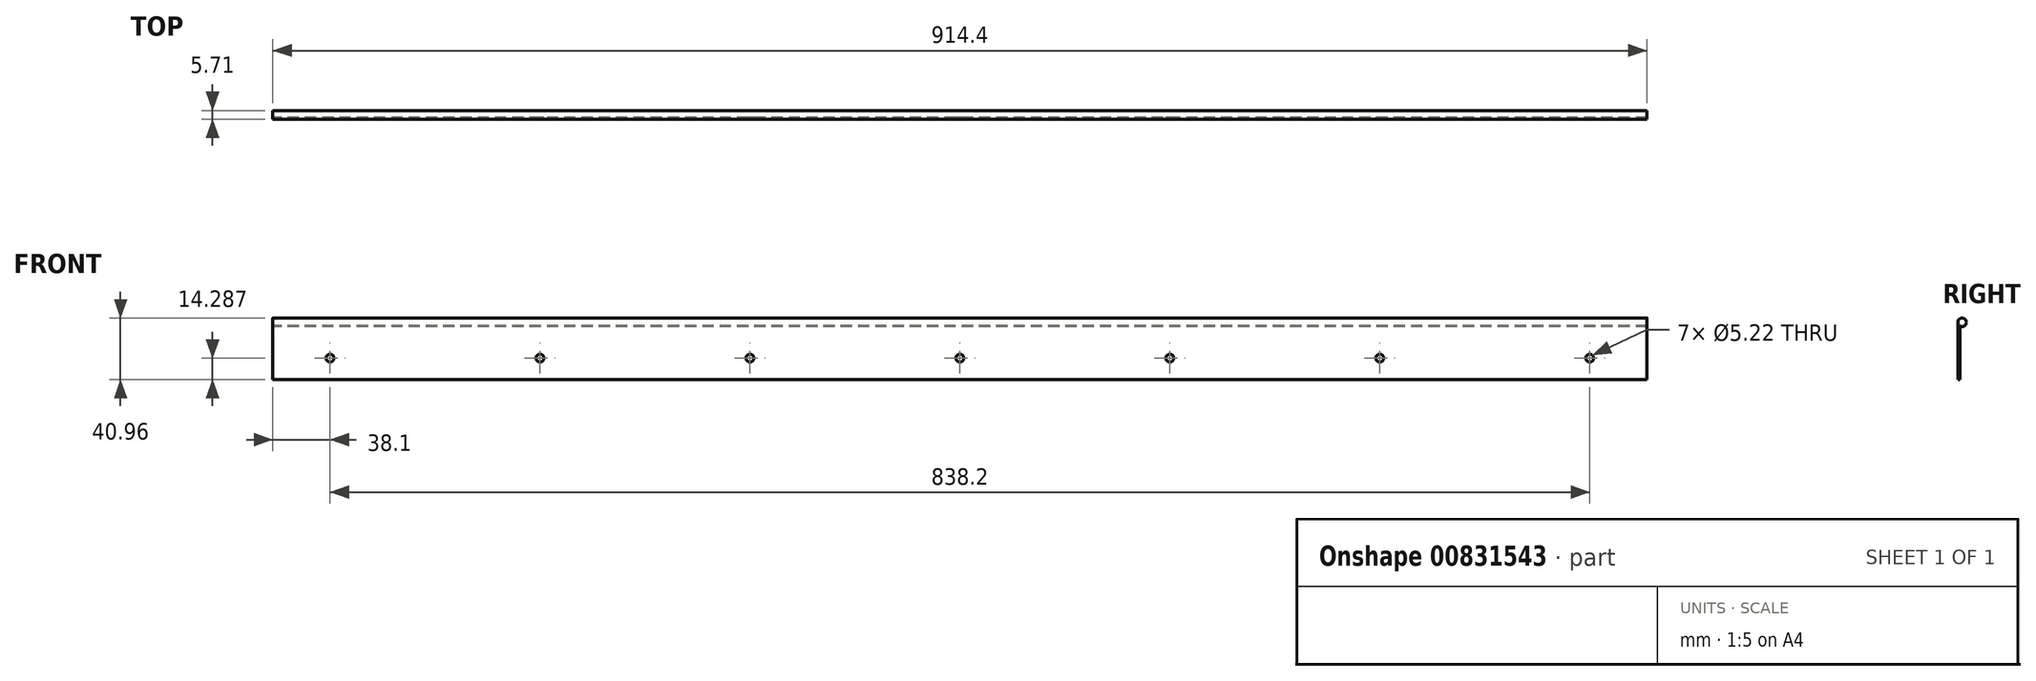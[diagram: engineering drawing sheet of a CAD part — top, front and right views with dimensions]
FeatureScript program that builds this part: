
annotation { "Feature Type Name" : "Feature", "Feature Type Description" : "" }
export const myFeature = defineFeature(function(context is Context, id is Id, definition is map)
    precondition{}
    {
        {
            var Q0;
            Q0=qCreatedBy(makeId("Right.planeOp"),FACE);
            var sketch = newSketch(context, id + "F0", { "sketchPlane" : qUnion([Q0])});
            skLineSegment(sketch, "E0.bottom", {"start": v(0, 0) * mm, "end": v(1.27, 0) * mm});
            skLineSegment(sketch, "E0.left", {"start": v(0, 0) * mm, "end": v(0, 38.1) * mm});
            skLineSegment(sketch, "E0.right", {"start": v(1.27, 0) * mm, "end": v(1.27, 35.72) * mm});
            skCircle(sketch, "E1", {"center": v(2.86, 38.1) * mm, "radius": 2.86 * mm, "construction": true});
            skPoint(sketch, "E1.centerSnap0", {"position": v(1.45, 38.1) * mm});
            skArc(sketch, "E2", {"start": v(1.27, 35.72) * mm, "mid": v(5.38, 39.45) * mm, "end": v(0, 38.1) * mm});
            skSolve(sketch);
        }
        {
            var Q0;
            Q0 = qSketchRegion(id + "F0", true);
            extrude(context, id + "F1", {"entities" : qUnion([Q0]), "depth" : 914.4 * mm, "offsetDistance" : 25.4 * mm});
        }
        {
            var Q0;
            Q0=makeQuery(id+"F1.opExtrude","SWEPT_FACE",FACE,{"disambiguationData":[OSD([sQuery(id+"F0.wireOp",EDGE,"E0.left")])]});
            var sketch = newSketch(context, id + "F2", { "sketchPlane" : qUnion([Q0])});
            skPoint(sketch, "E3", {"position": v(38.1, 14.29) * mm});
            skPoint(sketch, "E4", {"position": v(177.8, 14.29) * mm});
            skPoint(sketch, "E5", {"position": v(317.5, 14.29) * mm});
            skPoint(sketch, "E6", {"position": v(457.2, 14.29) * mm});
            skPoint(sketch, "E7", {"position": v(596.9, 14.29) * mm});
            skPoint(sketch, "E8", {"position": v(736.6, 14.29) * mm});
            skPoint(sketch, "E9", {"position": v(876.3, 14.29) * mm});
            skLineSegment(sketch, "E10", {"start": v(0, 14.29) * mm, "end": v(38.1, 14.29) * mm});
            skLineSegment(sketch, "E11", {"start": v(38.1, 14.29) * mm, "end": v(177.8, 14.29) * mm});
            skLineSegment(sketch, "E12", {"start": v(177.8, 14.29) * mm, "end": v(317.5, 14.29) * mm});
            skLineSegment(sketch, "E13", {"start": v(317.5, 14.29) * mm, "end": v(457.2, 14.29) * mm});
            skLineSegment(sketch, "E14", {"start": v(457.2, 14.29) * mm, "end": v(596.9, 14.29) * mm});
            skLineSegment(sketch, "E15", {"start": v(596.9, 14.29) * mm, "end": v(736.6, 14.29) * mm});
            skLineSegment(sketch, "E16", {"start": v(736.6, 14.29) * mm, "end": v(876.3, 14.29) * mm});
            skLineSegment(sketch, "E17", {"start": v(876.3, 14.29) * mm, "end": v(914.4, 14.29) * mm});
            skSolve(sketch);
        }
        {
            var Q0;
            Q0=sQuery(id+"F2.wireOp",VERTEX,"E3");
            var Q1;
            Q1=sQuery(id+"F2.wireOp",VERTEX,"E4");
            var Q2;
            Q2=sQuery(id+"F2.wireOp",VERTEX,"E5");
            var Q3;
            Q3=sQuery(id+"F2.wireOp",VERTEX,"E7");
            var Q4;
            Q4=sQuery(id+"F2.wireOp",VERTEX,"E8");
            var Q5;
            Q5=sQuery(id+"F2.wireOp",VERTEX,"E9");
            var Q6;
            Q6=sQuery(id+"F2.wireOp",VERTEX,"E6");
            var Q7;
            Q7=makeQuery(id+"F1.opExtrude","SWEPT_BODY",BODY,{"disambiguationData":[OSD([sQuery(id+"F0.wireOp",EDGE,"E0.bottom"),sQuery(id+"F0.wireOp",EDGE,"E0.left"),sQuery(id+"F0.wireOp",EDGE,"E0.right"),sQuery(id+"F0.wireOp",EDGE,"E2")])]});
            hole(context, id + "F3", {"style" : HoleStyle.SIMPLE, "endStyle" : HoleEndStyle.THROUGH, "standardTappedOrClearance" : lookupTablePath({ "standard" : "ANSI", "size" : "#5 (0.2)", "type" : "Drilled" }), "standardBlindInLast" : lookupTablePath({ "standard" : "ANSI", "size" : "#5 (0.2)", "type" : "Drilled" }), "holeDiameter" : 5.22 * mm, "majorDiameter" : 6.35 * mm, "isTappedThrough" : true, "tappedDepth" : 12.7 * mm, "tapClearance" : 3, "locations" : qUnion([Q0, Q1, Q2, Q3, Q4, Q5, Q6]), "scope" : qUnion([Q7])});
        }
    });
